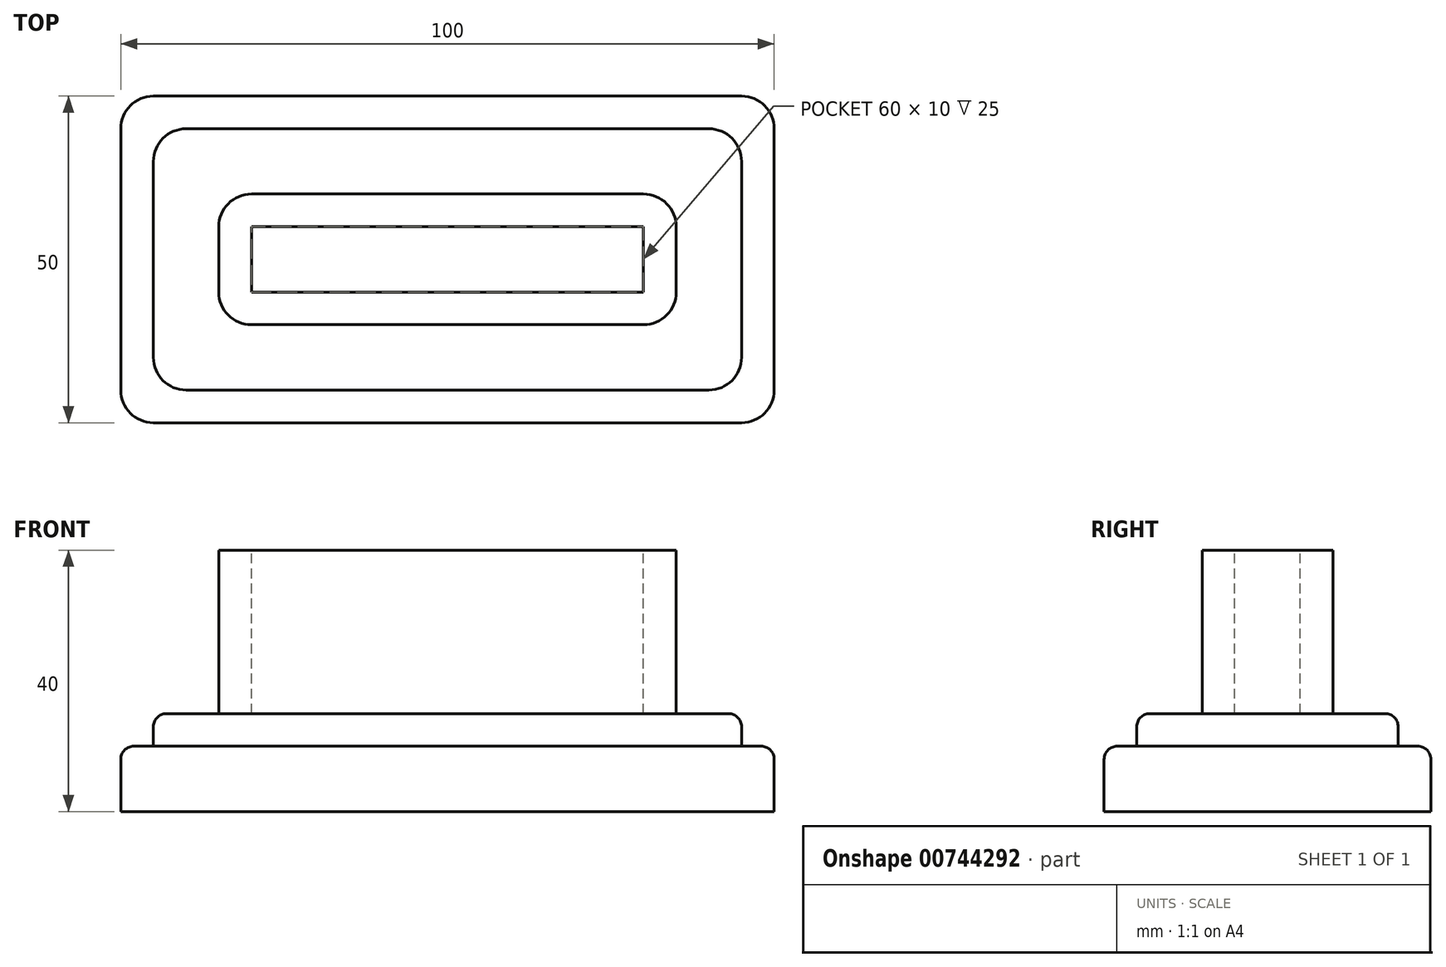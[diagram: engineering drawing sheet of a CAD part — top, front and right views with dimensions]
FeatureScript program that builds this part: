
annotation { "Feature Type Name" : "Feature", "Feature Type Description" : "" }
export const myFeature = defineFeature(function(context is Context, id is Id, definition is map)
    precondition{}
    {
        {
            var Q0;
            Q0=qCreatedBy(makeId("Top.planeOp"),FACE);
            var sketch = newSketch(context, id + "F0", { "sketchPlane" : qUnion([Q0])});
            skLineSegment(sketch, "E0.bottom", {"start": v(-47.52, 26.45) * mm, "end": v(52.48, 26.45) * mm});
            skLineSegment(sketch, "E0.top", {"start": v(-47.52, -23.55) * mm, "end": v(52.48, -23.55) * mm});
            skLineSegment(sketch, "E0.left", {"start": v(-47.52, 26.45) * mm, "end": v(-47.52, -23.55) * mm});
            skLineSegment(sketch, "E0.right", {"start": v(52.48, 26.45) * mm, "end": v(52.48, -23.55) * mm});
            skSolve(sketch);
        }
        {
            var Q0;
            Q0=makeQuery(id+"F0.imprint","IMPRINT",FACE,{"disambiguationData":[TD([[makeQuery(id+"F0.imprint","IMPRINT",EDGE,{"derivedFrom":sQuery(id+"F0.wireOp",EDGE,"E0.bottom")}),-1.0]])]});
            extrude(context, id + "F1", {"entities" : qUnion([Q0]), "depth" : 10 * mm, "offsetDistance" : 25 * mm});
        }
        {
            var Q0;
            Q0=makeQuery(id+"F1.opExtrude","CAP_FACE",FACE,{"disambiguationData":[OSD([sQuery(id+"F0.wireOp",EDGE,"E0.bottom"),sQuery(id+"F0.wireOp",EDGE,"E0.top"),sQuery(id+"F0.wireOp",EDGE,"E0.left"),sQuery(id+"F0.wireOp",EDGE,"E0.right")])],"isStart":false});
            var sketch = newSketch(context, id + "F2", { "sketchPlane" : qUnion([Q0])});
            skLineSegment(sketch, "E1.bottom", {"start": v(-42.52, 21.45) * mm, "end": v(47.48, 21.45) * mm});
            skLineSegment(sketch, "E1.top", {"start": v(-42.52, -18.55) * mm, "end": v(47.48, -18.55) * mm});
            skLineSegment(sketch, "E1.left", {"start": v(-42.52, 21.45) * mm, "end": v(-42.52, -18.55) * mm});
            skLineSegment(sketch, "E1.right", {"start": v(47.48, 21.45) * mm, "end": v(47.48, -18.55) * mm});
            skSolve(sketch);
        }
        {
            var Q0;
            Q0=makeQuery(id+"F2.imprint","IMPRINT",FACE,{"disambiguationData":[TD([[makeQuery(id+"F2.imprint","IMPRINT",EDGE,{"derivedFrom":sQuery(id+"F2.wireOp",EDGE,"E1.bottom")}),-1.0]])]});
            extrude(context, id + "F3", {"entities" : qUnion([Q0]), "operationType" : NewBodyOperationType.ADD, "depth" : 5 * mm, "offsetDistance" : 25 * mm});
        }
        {
            var Q0;
            Q0=makeQuery(id+"F3.opExtrude","CAP_FACE",FACE,{"disambiguationData":[OSD([sQuery(id+"F2.wireOp",EDGE,"E1.bottom"),sQuery(id+"F2.wireOp",EDGE,"E1.top"),sQuery(id+"F2.wireOp",EDGE,"E1.left"),sQuery(id+"F2.wireOp",EDGE,"E1.right")])],"isStart":false});
            var sketch = newSketch(context, id + "F4", { "sketchPlane" : qUnion([Q0])});
            skLineSegment(sketch, "E2.bottom", {"start": v(-32.52, 11.45) * mm, "end": v(37.48, 11.45) * mm});
            skLineSegment(sketch, "E2.top", {"start": v(-32.52, -8.55) * mm, "end": v(37.48, -8.55) * mm});
            skLineSegment(sketch, "E2.left", {"start": v(-32.52, 11.45) * mm, "end": v(-32.52, -8.55) * mm});
            skLineSegment(sketch, "E2.right", {"start": v(37.48, 11.45) * mm, "end": v(37.48, -8.55) * mm});
            skSolve(sketch);
        }
        {
            var Q0;
            Q0=makeQuery(id+"F4.imprint","IMPRINT",FACE,{"disambiguationData":[TD([[makeQuery(id+"F4.imprint","IMPRINT",EDGE,{"derivedFrom":sQuery(id+"F4.wireOp",EDGE,"E2.bottom")}),-1.0]])]});
            extrude(context, id + "F5", {"entities" : qUnion([Q0]), "operationType" : NewBodyOperationType.ADD, "depth" : 25 * mm, "offsetDistance" : 25 * mm});
        }
        {
            var Q0;
            Q0=makeQuery(id+"F5.opExtrude","CAP_FACE",FACE,{"disambiguationData":[OSD([sQuery(id+"F4.wireOp",EDGE,"E2.bottom"),sQuery(id+"F4.wireOp",EDGE,"E2.top"),sQuery(id+"F4.wireOp",EDGE,"E2.left"),sQuery(id+"F4.wireOp",EDGE,"E2.right")])],"isStart":false});
            var sketch = newSketch(context, id + "F6", { "sketchPlane" : qUnion([Q0])});
            skLineSegment(sketch, "E3.bottom", {"start": v(-27.52, 6.45) * mm, "end": v(32.48, 6.45) * mm});
            skLineSegment(sketch, "E3.top", {"start": v(-27.52, -3.55) * mm, "end": v(32.48, -3.55) * mm});
            skLineSegment(sketch, "E3.left", {"start": v(-27.52, 6.45) * mm, "end": v(-27.52, -3.55) * mm});
            skLineSegment(sketch, "E3.right", {"start": v(32.48, 6.45) * mm, "end": v(32.48, -3.55) * mm});
            skSolve(sketch);
        }
        {
            var Q0;
            Q0=makeQuery(id+"F6.imprint","IMPRINT",FACE,{"disambiguationData":[TD([[makeQuery(id+"F6.imprint","IMPRINT",EDGE,{"derivedFrom":sQuery(id+"F6.wireOp",EDGE,"E3.bottom")}),-1.0]])]});
            extrude(context, id + "F7", {"entities" : qUnion([Q0]), "operationType" : NewBodyOperationType.REMOVE, "oppositeDirection" : true, "depth" : 25 * mm, "offsetDistance" : 25 * mm});
        }
        {
            var Q0;
            Q0=makeQuery(id+"F5.opExtrude","SWEPT_EDGE",EDGE,{"disambiguationData":[OSD([sQuery(id+"F4.wireOp",EDGE,"E2.top"),sQuery(id+"F4.wireOp",EDGE,"E2.right")])]});
            var Q1;
            Q1=makeQuery(id+"F5.opExtrude","SWEPT_EDGE",EDGE,{"disambiguationData":[OSD([sQuery(id+"F4.wireOp",EDGE,"E2.bottom"),sQuery(id+"F4.wireOp",EDGE,"E2.right")])]});
            var Q2;
            Q2=makeQuery(id+"F5.opExtrude","SWEPT_EDGE",EDGE,{"disambiguationData":[OSD([sQuery(id+"F4.wireOp",EDGE,"E2.top"),sQuery(id+"F4.wireOp",EDGE,"E2.left")])]});
            var Q3;
            Q3=makeQuery(id+"F5.opExtrude","SWEPT_EDGE",EDGE,{"disambiguationData":[OSD([sQuery(id+"F4.wireOp",EDGE,"E2.bottom"),sQuery(id+"F4.wireOp",EDGE,"E2.left")])]});
            fillet(context, id + "F8", {"entities" : qUnion([Q0, Q1, Q2, Q3]), "radius" : 5 * mm, "tangentPropagation" : true, "allowEdgeOverflow" : false});
        }
        {
            var Q0;
            Q0=makeQuery(id+"F1.opExtrude","SWEPT_EDGE",EDGE,{"disambiguationData":[OSD([sQuery(id+"F0.wireOp",EDGE,"E0.bottom"),sQuery(id+"F0.wireOp",EDGE,"E0.right")])]});
            var Q1;
            Q1=makeQuery(id+"F1.opExtrude","SWEPT_EDGE",EDGE,{"disambiguationData":[OSD([sQuery(id+"F0.wireOp",EDGE,"E0.top"),sQuery(id+"F0.wireOp",EDGE,"E0.left")])]});
            var Q2;
            Q2=makeQuery(id+"F1.opExtrude","SWEPT_EDGE",EDGE,{"disambiguationData":[OSD([sQuery(id+"F0.wireOp",EDGE,"E0.bottom"),sQuery(id+"F0.wireOp",EDGE,"E0.left")])]});
            var Q3;
            Q3=makeQuery(id+"F1.opExtrude","SWEPT_EDGE",EDGE,{"disambiguationData":[OSD([sQuery(id+"F0.wireOp",EDGE,"E0.top"),sQuery(id+"F0.wireOp",EDGE,"E0.right")])]});
            fillet(context, id + "F9", {"entities" : qUnion([Q0, Q1, Q2, Q3]), "radius" : 5 * mm, "tangentPropagation" : true, "allowEdgeOverflow" : false});
        }
        {
            var Q0;
            Q0=makeQuery(id+"F3.opExtrude","SWEPT_EDGE",EDGE,{"disambiguationData":[OSD([sQuery(id+"F2.wireOp",EDGE,"E1.top"),sQuery(id+"F2.wireOp",EDGE,"E1.right")])]});
            var Q1;
            Q1=makeQuery(id+"F3.opExtrude","SWEPT_EDGE",EDGE,{"disambiguationData":[OSD([sQuery(id+"F2.wireOp",EDGE,"E1.top"),sQuery(id+"F2.wireOp",EDGE,"E1.left")])]});
            var Q2;
            Q2=makeQuery(id+"F3.opExtrude","SWEPT_EDGE",EDGE,{"disambiguationData":[OSD([sQuery(id+"F2.wireOp",EDGE,"E1.bottom"),sQuery(id+"F2.wireOp",EDGE,"E1.right")])]});
            var Q3;
            Q3=makeQuery(id+"F3.opExtrude","SWEPT_EDGE",EDGE,{"disambiguationData":[OSD([sQuery(id+"F2.wireOp",EDGE,"E1.bottom"),sQuery(id+"F2.wireOp",EDGE,"E1.left")])]});
            fillet(context, id + "F10", {"entities" : qUnion([Q0, Q1, Q2, Q3]), "radius" : 5 * mm, "tangentPropagation" : true, "allowEdgeOverflow" : false});
        }
        {
            var Q0;
            Q0=makeQuery(id+"F5.opExtrude","CAP_EDGE",EDGE,{"disambiguationData":[OSD([sQuery(id+"F4.wireOp",EDGE,"E2.bottom")])],"isStart":true});
            var Q1;
            Q1=makeQuery(id+"F3.opExtrude","CAP_EDGE",EDGE,{"disambiguationData":[OSD([sQuery(id+"F2.wireOp",EDGE,"E1.bottom")])],"isStart":false});
            var Q2;
            Q2=makeQuery(id+"F3.opExtrude","CAP_EDGE",EDGE,{"disambiguationData":[OSD([sQuery(id+"F2.wireOp",EDGE,"E1.bottom")])],"isStart":true});
            var Q3;
            Q3=makeQuery(id+"F1.opExtrude","CAP_EDGE",EDGE,{"disambiguationData":[OSD([sQuery(id+"F0.wireOp",EDGE,"E0.bottom")])],"isStart":false});
            fillet(context, id + "F11", {"entities" : qUnion([Q0, Q1, Q2, Q3]), "radius" : 2 * mm, "tangentPropagation" : true, "allowEdgeOverflow" : false});
        }
    });
